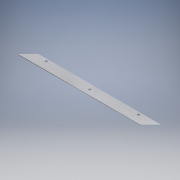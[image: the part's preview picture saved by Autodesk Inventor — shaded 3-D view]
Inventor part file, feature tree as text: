
AUTODESK INVENTOR PART (.ipt)
format: ipt  version: 2016 (Build 200138000, 138)  size: 123,392 bytes
history: native  units: in
note: dims shown in document units (in); Inventor stores cm internally (conversion verified against a paired STEP export)
features: extrude x2, sketch x2
ambient origin geometry x8: Origin, YZ Plane, XZ Plane, XY Plane, X Axis, Y Axis, Z Axis, Center Point
bodies: Solid1 (feature_tree)
feature tree (4):
  extrude  "Extrusion1"  Depth=2.0in
  extrude  "Extrusion2"  Depth=0.125in
  sketch  "Sketch1"  dims[d0=30.0in d1=2.0in]
  sketch  "Sketch2"  dims[d2=0.125in d3=0.0in d4=0.5in d5=1.0in d6=15.0in d7=0.125in d8=0.0in d9=0.5in d10=1.5in d11=9.0in d12=0.5in d13=1.5in d14=9.0in]
